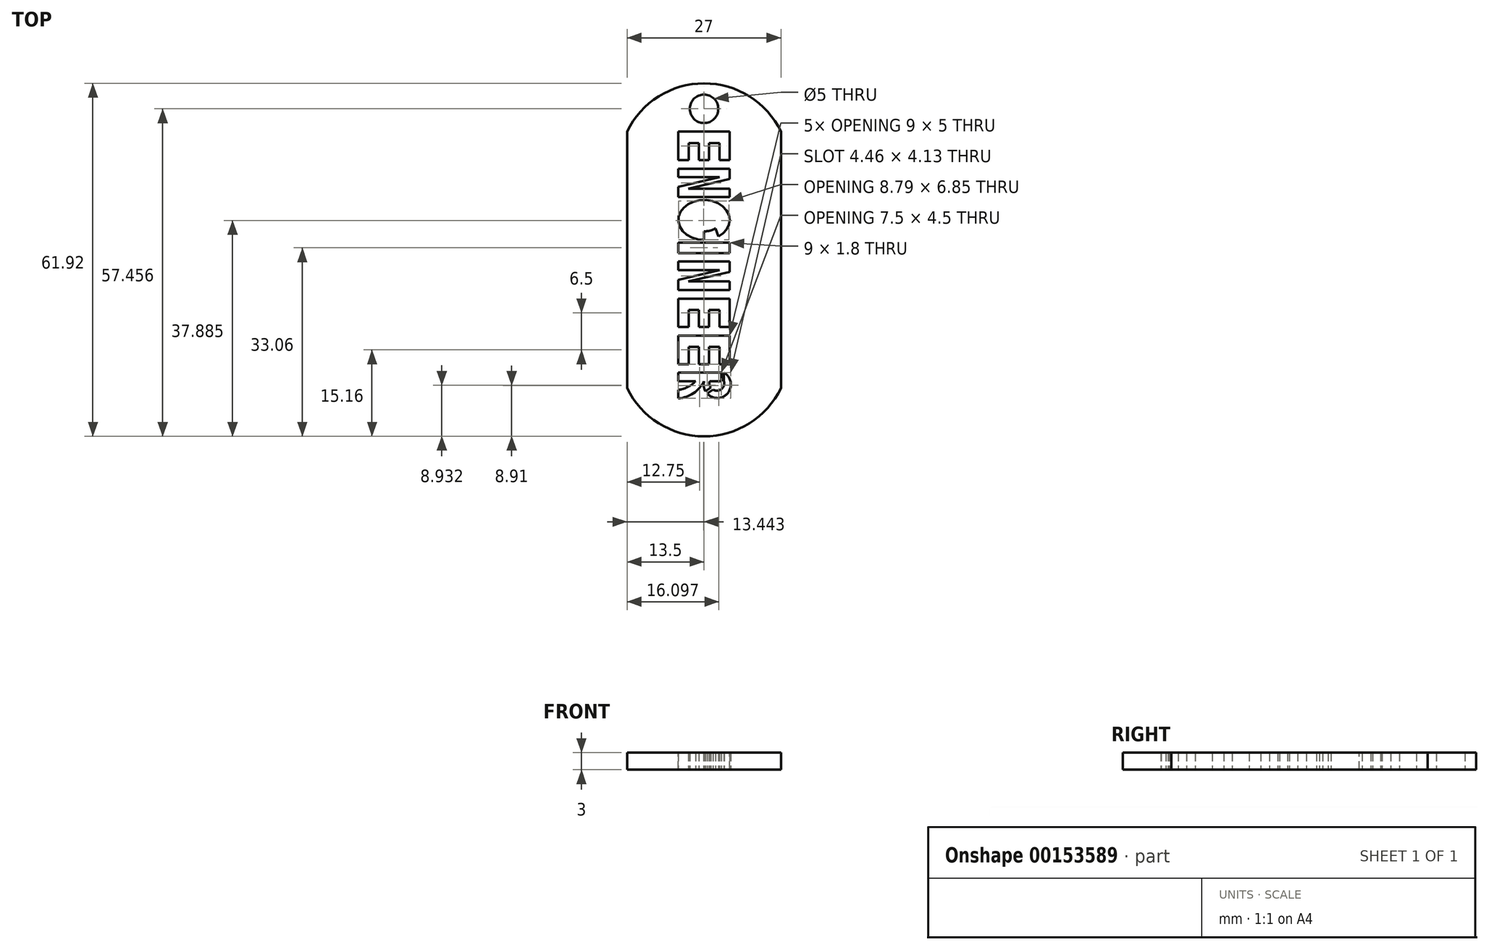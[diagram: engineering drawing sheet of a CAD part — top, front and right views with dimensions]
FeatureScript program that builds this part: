
annotation { "Feature Type Name" : "Feature", "Feature Type Description" : "" }
export const myFeature = defineFeature(function(context is Context, id is Id, definition is map)
    precondition{}
    {
        {
            var Q0;
            Q0=qCreatedBy(makeId("Top.planeOp"),FACE);
            var sketch = newSketch(context, id + "F0", { "sketchPlane" : qUnion([Q0])});
            skLineSegment(sketch, "E0", {"start": v(0, 0) * mm, "end": v(0, -45) * mm});
            skArc(sketch, "E1", {"start": v(27, 0) * mm, "mid": v(13.5, 8.46) * mm, "end": v(0, 0) * mm});
            skLineSegment(sketch, "E2", {"start": v(27, 0) * mm, "end": v(27, -45) * mm});
            skArc(sketch, "E3", {"start": v(0, -45) * mm, "mid": v(13.5, -53.46) * mm, "end": v(27, -45) * mm});
            skLineSegment(sketch, "E4", {"start": v(9, 0) * mm, "end": v(9, -5) * mm});
            skLineSegment(sketch, "E5", {"start": v(9, -5) * mm, "end": v(10.8, -5) * mm});
            skLineSegment(sketch, "E6", {"start": v(10.8, -2) * mm, "end": v(12.6, -2) * mm});
            skLineSegment(sketch, "E7", {"start": v(12.6, -2) * mm, "end": v(12.6, -5) * mm});
            skLineSegment(sketch, "E8", {"start": v(12.6, -5) * mm, "end": v(14.4, -5) * mm});
            skLineSegment(sketch, "E9", {"start": v(14.4, -5) * mm, "end": v(14.4, -2) * mm});
            skLineSegment(sketch, "E10", {"start": v(16.2, -2) * mm, "end": v(16.2, -5) * mm});
            skLineSegment(sketch, "E11", {"start": v(16.2, -5) * mm, "end": v(18, -5) * mm});
            skLineSegment(sketch, "E12", {"start": v(18, -5) * mm, "end": v(18, 0) * mm});
            skLineSegment(sketch, "E13", {"start": v(18, 0) * mm, "end": v(9, 0) * mm});
            skLineSegment(sketch, "E14", {"start": v(16.2, -2) * mm, "end": v(14.4, -2) * mm});
            skLineSegment(sketch, "E15", {"start": v(10.8, -2) * mm, "end": v(10.8, -5) * mm});
            skLineSegment(sketch, "E16", {"start": v(9, -6.5) * mm, "end": v(9, -8) * mm});
            skLineSegment(sketch, "E17", {"start": v(9, -8) * mm, "end": v(16.22, -8) * mm});
            skLineSegment(sketch, "E18", {"start": v(16.22, -8) * mm, "end": v(9, -9.7) * mm});
            skLineSegment(sketch, "E19", {"start": v(9, -9.7) * mm, "end": v(9, -11.5) * mm});
            skLineSegment(sketch, "E20", {"start": v(9, -11.5) * mm, "end": v(18, -11.5) * mm});
            skLineSegment(sketch, "E21", {"start": v(18, -11.5) * mm, "end": v(18, -10) * mm});
            skLineSegment(sketch, "E22", {"start": v(18, -10) * mm, "end": v(10.78, -10) * mm});
            skLineSegment(sketch, "E23", {"start": v(10.78, -10) * mm, "end": v(18, -8.3) * mm});
            skLineSegment(sketch, "E24", {"start": v(18, -8.3) * mm, "end": v(18, -6.5) * mm});
            skLineSegment(sketch, "E25", {"start": v(18, -6.5) * mm, "end": v(9, -6.5) * mm});
            skEllipse(sketch, "E26", {"center": v(13.5, -15.5) * mm, "majorRadius": 4.5 * mm, "minorRadius": 3.5 * mm, "majorAxis": v(1, 0)});
            skEllipse(sketch, "E27", {"center": v(13.5, -15.5) * mm, "majorRadius": 3 * mm, "minorRadius": 2 * mm, "majorAxis": v(1, 0)});
            skLineSegment(sketch, "E28", {"start": v(13.5, -19) * mm, "end": v(13.5, -16) * mm});
            skPoint(sketch, "E28.endSnap0", {"position": v(13.5, -17.5) * mm});
            skLineSegment(sketch, "E29", {"start": v(13.5, -16) * mm, "end": v(12.17, -16) * mm});
            skLineSegment(sketch, "E30", {"start": v(12.17, -16) * mm, "end": v(12.17, -18.84) * mm});
            skLineSegment(sketch, "E31", {"start": v(16, -18.41) * mm, "end": v(15.5, -17) * mm});
            skLineSegment(sketch, "E32", {"start": v(18, -19.5) * mm, "end": v(9, -19.5) * mm});
            skLineSegment(sketch, "E33", {"start": v(9, -19.5) * mm, "end": v(9, -21.3) * mm});
            skLineSegment(sketch, "E34", {"start": v(9, -21.3) * mm, "end": v(18, -21.3) * mm});
            skLineSegment(sketch, "E35", {"start": v(18, -21.3) * mm, "end": v(18, -19.5) * mm});
            skLineSegment(sketch, "E36", {"start": v(9, -22.8) * mm, "end": v(9, -24.3) * mm});
            skLineSegment(sketch, "E37", {"start": v(9, -24.3) * mm, "end": v(16.22, -24.3) * mm});
            skLineSegment(sketch, "E38", {"start": v(16.22, -24.3) * mm, "end": v(9, -26) * mm});
            skLineSegment(sketch, "E39", {"start": v(9, -26) * mm, "end": v(9, -27.8) * mm});
            skLineSegment(sketch, "E40", {"start": v(9, -27.8) * mm, "end": v(18, -27.8) * mm});
            skLineSegment(sketch, "E41", {"start": v(18, -27.8) * mm, "end": v(18, -26.3) * mm});
            skLineSegment(sketch, "E42", {"start": v(18, -26.3) * mm, "end": v(10.78, -26.3) * mm});
            skLineSegment(sketch, "E43", {"start": v(10.78, -26.3) * mm, "end": v(18, -24.6) * mm});
            skLineSegment(sketch, "E44", {"start": v(18, -24.6) * mm, "end": v(18, -22.8) * mm});
            skLineSegment(sketch, "E45", {"start": v(18, -22.8) * mm, "end": v(9, -22.8) * mm});
            skLineSegment(sketch, "E46", {"start": v(9, -29.3) * mm, "end": v(9, -34.3) * mm});
            skLineSegment(sketch, "E47", {"start": v(9, -34.3) * mm, "end": v(10.8, -34.3) * mm});
            skLineSegment(sketch, "E48", {"start": v(10.8, -31.3) * mm, "end": v(12.6, -31.3) * mm});
            skLineSegment(sketch, "E49", {"start": v(12.6, -31.3) * mm, "end": v(12.6, -34.3) * mm});
            skLineSegment(sketch, "E50", {"start": v(12.6, -34.3) * mm, "end": v(14.4, -34.3) * mm});
            skLineSegment(sketch, "E51", {"start": v(14.4, -34.3) * mm, "end": v(14.4, -31.3) * mm});
            skLineSegment(sketch, "E52", {"start": v(16.2, -31.3) * mm, "end": v(16.2, -34.3) * mm});
            skLineSegment(sketch, "E53", {"start": v(16.2, -34.3) * mm, "end": v(18, -34.3) * mm});
            skLineSegment(sketch, "E54", {"start": v(18, -34.3) * mm, "end": v(18, -29.3) * mm});
            skLineSegment(sketch, "E55", {"start": v(18, -29.3) * mm, "end": v(9, -29.3) * mm});
            skLineSegment(sketch, "E56", {"start": v(16.2, -31.3) * mm, "end": v(14.4, -31.3) * mm});
            skLineSegment(sketch, "E57", {"start": v(10.8, -31.3) * mm, "end": v(10.8, -34.3) * mm});
            skLineSegment(sketch, "E58", {"start": v(18, -35.8) * mm, "end": v(9, -35.8) * mm});
            skLineSegment(sketch, "E59", {"start": v(9, -35.8) * mm, "end": v(9, -40.8) * mm});
            skLineSegment(sketch, "E60", {"start": v(9, -40.8) * mm, "end": v(10.8, -40.8) * mm});
            skLineSegment(sketch, "E61", {"start": v(10.8, -40.8) * mm, "end": v(10.8, -37.8) * mm});
            skLineSegment(sketch, "E62", {"start": v(10.8, -37.8) * mm, "end": v(12.6, -37.8) * mm});
            skLineSegment(sketch, "E63", {"start": v(12.6, -37.8) * mm, "end": v(12.6, -40.8) * mm});
            skLineSegment(sketch, "E64", {"start": v(12.6, -40.8) * mm, "end": v(14.4, -40.8) * mm});
            skLineSegment(sketch, "E65", {"start": v(14.4, -40.8) * mm, "end": v(14.4, -37.8) * mm});
            skLineSegment(sketch, "E66", {"start": v(14.4, -37.8) * mm, "end": v(16.2, -37.8) * mm});
            skLineSegment(sketch, "E67", {"start": v(16.2, -37.8) * mm, "end": v(16.2, -40.8) * mm});
            skLineSegment(sketch, "E68", {"start": v(16.2, -40.8) * mm, "end": v(18, -40.8) * mm});
            skLineSegment(sketch, "E69", {"start": v(18, -40.8) * mm, "end": v(18, -35.8) * mm});
            skLineSegment(sketch, "E70", {"start": v(9, -42.3) * mm, "end": v(17, -42.3) * mm});
            skLineSegment(sketch, "E71", {"start": v(9, -42.3) * mm, "end": v(9, -43.8) * mm});
            skLineSegment(sketch, "E72", {"start": v(9, -43.8) * mm, "end": v(12, -43.8) * mm});
            skArc(sketch, "E73", {"start": v(9, -45.3) * mm, "mid": v(10.63, -44.82) * mm, "end": v(12, -43.8) * mm});
            skLineSegment(sketch, "E74", {"start": v(12, -43.8) * mm, "end": v(13.5, -43.8) * mm});
            skLineSegment(sketch, "E75", {"start": v(9, -45.3) * mm, "end": v(9, -46.8) * mm});
            skArc(sketch, "E76", {"start": v(9, -46.8) * mm, "mid": v(11.64, -45.9) * mm, "end": v(13.5, -43.8) * mm});
            skLineSegment(sketch, "E77", {"start": v(13.5, -43.8) * mm, "end": v(14.5, -43.8) * mm});
            skLineSegment(sketch, "E78", {"start": v(17, -42.3) * mm, "end": v(17, -43.8) * mm});
            skArc(sketch, "E79", {"start": v(14.5, -43.8) * mm, "mid": v(15.75, -45.46) * mm, "end": v(17, -43.8) * mm});
            skLineSegment(sketch, "E80", {"start": v(17, -43.8) * mm, "end": v(14.5, -43.8) * mm});
            skLineSegment(sketch, "E81", {"start": v(13.5, -17.5) * mm, "end": v(13.5, -19) * mm});
            skArc(sketch, "E82", {"start": v(13.5, -43.8) * mm, "mid": v(16.76, -46.56) * mm, "end": v(17, -42.3) * mm});
            skLineSegment(sketch, "E83", {"start": v(16.5, -42.3) * mm, "end": v(16.5, -43.8) * mm});
            skLineSegment(sketch, "E84", {"start": v(14.68, -44.9) * mm, "end": v(13.74, -45.55) * mm});
            skLineSegment(sketch, "E85", {"start": v(15.05, -45.25) * mm, "end": v(14.03, -45.96) * mm});
            skCircle(sketch, "E86", {"center": v(13.5, 4) * mm, "radius": 2.5 * mm});
            skSolve(sketch);
        }
        {
            var Q0;
            Q0 = qSketchRegion(id + "F0", true);
            var Q1;
            {var subQ1=sQuery(id+"F0.wireOp",EDGE,"E28");Q1=makeQuery(id+"F0.imprint","IMPRINT",FACE,{"disambiguationData":[TD([[makeQuery(id+"F0.imprint","IMPRINT",EDGE,{"derivedFrom":subQ1}),-1.0]])]});}
            var Q2;
            {var subQ0=sQuery(id+"F0.wireOp",EDGE,"E31");Q2=makeQuery(id+"F0.imprint","IMPRINT",FACE,{"disambiguationData":[TD([[makeQuery(id+"F0.imprint","IMPRINT",EDGE,{"derivedFrom":subQ0}),1.0]])]});}
            var Q3;
            Q3=makeQuery(id+"F0.imprint","IMPRINT",FACE,{"disambiguationData":[TD([[makeQuery(id+"F0.imprint","IMPRINT",EDGE,{"derivedFrom":sQuery(id+"F0.wireOp",EDGE,"E79")}),1.0]])]});
            var Q4;
            {var subQ0=sQuery(id+"F0.wireOp",EDGE,"E78");Q4=makeQuery(id+"F0.imprint","IMPRINT",FACE,{"disambiguationData":[TD([[makeQuery(id+"F0.imprint","IMPRINT",EDGE,{"derivedFrom":subQ0}),-1.0]])]});}
            var Q5;
            {var subQ0=sQuery(id+"F0.wireOp",EDGE,"E84");Q5=makeQuery(id+"F0.imprint","IMPRINT",FACE,{"disambiguationData":[TD([[makeQuery(id+"F0.imprint","IMPRINT",EDGE,{"derivedFrom":subQ0}),1.0]])]});}
            extrude(context, id + "F1", {"entities" : qUnion([Q0, Q1, Q2, Q3, Q4, Q5]), "depth" : 3 * mm});
        }
    });
